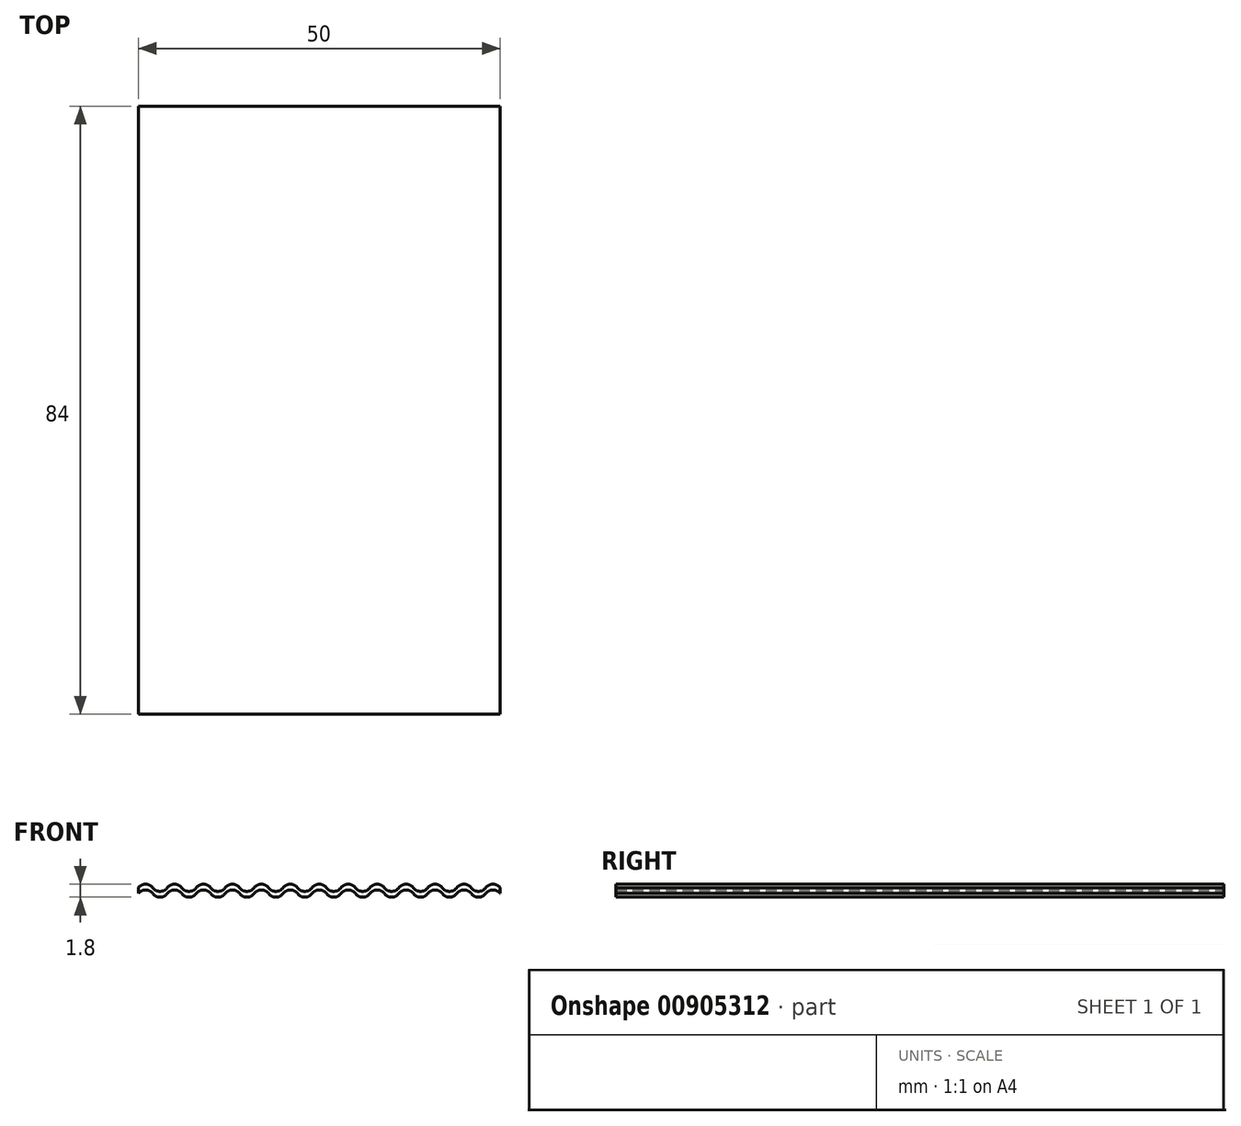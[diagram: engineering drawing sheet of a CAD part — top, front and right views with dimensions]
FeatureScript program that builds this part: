
annotation { "Feature Type Name" : "Feature", "Feature Type Description" : "" }
export const myFeature = defineFeature(function(context is Context, id is Id, definition is map)
    precondition{}
    {
        {
            var Q0;
            Q0=qCreatedBy(makeId("Front.planeOp"),FACE);
            var sketch = newSketch(context, id + "F0", { "sketchPlane" : qUnion([Q0])});
            skArc(sketch, "E0", {"start": v(-19, -0.4) * mm, "mid": v(-20, 0.1) * mm, "end": v(-21, -0.4) * mm});
            skArc(sketch, "E1", {"start": v(-23, -0.4) * mm, "mid": v(-22, -0.9) * mm, "end": v(-21, -0.4) * mm});
            skArc(sketch, "E2", {"start": v(-23, -0.4) * mm, "mid": v(-24, 0.1) * mm, "end": v(-25, -0.4) * mm});
            skArc(sketch, "E3", {"start": v(5, -0.4) * mm, "mid": v(6, -0.9) * mm, "end": v(7, -0.4) * mm});
            skArc(sketch, "E4", {"start": v(9, -0.4) * mm, "mid": v(8, 0.1) * mm, "end": v(7, -0.4) * mm});
            skArc(sketch, "E5", {"start": v(9, -0.4) * mm, "mid": v(10, -0.9) * mm, "end": v(11, -0.4) * mm});
            skArc(sketch, "E6", {"start": v(13, -0.4) * mm, "mid": v(12, 0.1) * mm, "end": v(11, -0.4) * mm});
            skArc(sketch, "E7", {"start": v(13, -0.4) * mm, "mid": v(14, -0.9) * mm, "end": v(15, -0.4) * mm});
            skArc(sketch, "E8", {"start": v(17, -0.4) * mm, "mid": v(16, 0.1) * mm, "end": v(15, -0.4) * mm});
            skArc(sketch, "E9", {"start": v(25, -0.4) * mm, "mid": v(24, 0.1) * mm, "end": v(23, -0.4) * mm});
            skArc(sketch, "E10", {"start": v(21, -0.4) * mm, "mid": v(22, -0.9) * mm, "end": v(23, -0.4) * mm});
            skArc(sketch, "E11", {"start": v(21, -0.4) * mm, "mid": v(20, 0.1) * mm, "end": v(19, -0.4) * mm});
            skArc(sketch, "E12", {"start": v(17, -0.4) * mm, "mid": v(18, -0.9) * mm, "end": v(19, -0.4) * mm});
            skArc(sketch, "E13", {"start": v(5, -0.4) * mm, "mid": v(4, 0.1) * mm, "end": v(3, -0.4) * mm});
            skArc(sketch, "E14", {"start": v(1, -0.4) * mm, "mid": v(2, -0.9) * mm, "end": v(3, -0.4) * mm});
            skArc(sketch, "E15", {"start": v(1, -0.4) * mm, "mid": v(0, 0.1) * mm, "end": v(-1, -0.4) * mm});
            skArc(sketch, "E16", {"start": v(-3, -0.4) * mm, "mid": v(-2, -0.9) * mm, "end": v(-1, -0.4) * mm});
            skArc(sketch, "E17", {"start": v(-3, -0.4) * mm, "mid": v(-4, 0.1) * mm, "end": v(-5, -0.4) * mm});
            skArc(sketch, "E18", {"start": v(-7, -0.4) * mm, "mid": v(-6, -0.9) * mm, "end": v(-5, -0.4) * mm});
            skArc(sketch, "E19", {"start": v(-7, -0.4) * mm, "mid": v(-8, 0.1) * mm, "end": v(-9, -0.4) * mm});
            skArc(sketch, "E20", {"start": v(-11, -0.4) * mm, "mid": v(-10, -0.9) * mm, "end": v(-9, -0.4) * mm});
            skArc(sketch, "E21", {"start": v(-11, -0.4) * mm, "mid": v(-12, 0.1) * mm, "end": v(-13, -0.4) * mm});
            skArc(sketch, "E22", {"start": v(-15, -0.4) * mm, "mid": v(-14, -0.9) * mm, "end": v(-13, -0.4) * mm});
            skArc(sketch, "E23", {"start": v(-15, -0.4) * mm, "mid": v(-16, 0.1) * mm, "end": v(-17, -0.4) * mm});
            skArc(sketch, "E24", {"start": v(-19, -0.4) * mm, "mid": v(-18, -0.9) * mm, "end": v(-17, -0.4) * mm});
            skArc(sketch, "E25", {"start": v(-19, 0.4) * mm, "mid": v(-20, 0.9) * mm, "end": v(-21, 0.4) * mm});
            skArc(sketch, "E26", {"start": v(-23, 0.4) * mm, "mid": v(-22, -0.1) * mm, "end": v(-21, 0.4) * mm});
            skArc(sketch, "E27", {"start": v(-23, 0.4) * mm, "mid": v(-24, 0.9) * mm, "end": v(-25, 0.4) * mm});
            skArc(sketch, "E28", {"start": v(5, 0.4) * mm, "mid": v(6, -0.1) * mm, "end": v(7, 0.4) * mm});
            skArc(sketch, "E29", {"start": v(9, 0.4) * mm, "mid": v(8, 0.9) * mm, "end": v(7, 0.4) * mm});
            skArc(sketch, "E30", {"start": v(9, 0.4) * mm, "mid": v(10, -0.1) * mm, "end": v(11, 0.4) * mm});
            skArc(sketch, "E31", {"start": v(13, 0.4) * mm, "mid": v(12, 0.9) * mm, "end": v(11, 0.4) * mm});
            skArc(sketch, "E32", {"start": v(13, 0.4) * mm, "mid": v(14, -0.1) * mm, "end": v(15, 0.4) * mm});
            skArc(sketch, "E33", {"start": v(17, 0.4) * mm, "mid": v(16, 0.9) * mm, "end": v(15, 0.4) * mm});
            skArc(sketch, "E34", {"start": v(25, 0.4) * mm, "mid": v(24, 0.9) * mm, "end": v(23, 0.4) * mm});
            skArc(sketch, "E35", {"start": v(21, 0.4) * mm, "mid": v(22, -0.1) * mm, "end": v(23, 0.4) * mm});
            skArc(sketch, "E36", {"start": v(21, 0.4) * mm, "mid": v(20, 0.9) * mm, "end": v(19, 0.4) * mm});
            skArc(sketch, "E37", {"start": v(17, 0.4) * mm, "mid": v(18, -0.1) * mm, "end": v(19, 0.4) * mm});
            skArc(sketch, "E38", {"start": v(5, 0.4) * mm, "mid": v(4, 0.9) * mm, "end": v(3, 0.4) * mm});
            skArc(sketch, "E39", {"start": v(1, 0.4) * mm, "mid": v(2, -0.1) * mm, "end": v(3, 0.4) * mm});
            skArc(sketch, "E40", {"start": v(1, 0.4) * mm, "mid": v(0, 0.9) * mm, "end": v(-1, 0.4) * mm});
            skArc(sketch, "E41", {"start": v(-3, 0.4) * mm, "mid": v(-2, -0.1) * mm, "end": v(-1, 0.4) * mm});
            skArc(sketch, "E42", {"start": v(-3, 0.4) * mm, "mid": v(-4, 0.9) * mm, "end": v(-5, 0.4) * mm});
            skArc(sketch, "E43", {"start": v(-7, 0.4) * mm, "mid": v(-6, -0.1) * mm, "end": v(-5, 0.4) * mm});
            skArc(sketch, "E44", {"start": v(-7, 0.4) * mm, "mid": v(-8, 0.9) * mm, "end": v(-9, 0.4) * mm});
            skArc(sketch, "E45", {"start": v(-11, 0.4) * mm, "mid": v(-10, -0.1) * mm, "end": v(-9, 0.4) * mm});
            skArc(sketch, "E46", {"start": v(-11, 0.4) * mm, "mid": v(-12, 0.9) * mm, "end": v(-13, 0.4) * mm});
            skArc(sketch, "E47", {"start": v(-15, 0.4) * mm, "mid": v(-14, -0.1) * mm, "end": v(-13, 0.4) * mm});
            skArc(sketch, "E48", {"start": v(-15, 0.4) * mm, "mid": v(-16, 0.9) * mm, "end": v(-17, 0.4) * mm});
            skArc(sketch, "E49", {"start": v(-19, 0.4) * mm, "mid": v(-18, -0.1) * mm, "end": v(-17, 0.4) * mm});
            skLineSegment(sketch, "E50", {"start": v(-25, 0.4) * mm, "end": v(-25, -0.4) * mm});
            skLineSegment(sketch, "E51", {"start": v(25, 0.4) * mm, "end": v(25, -0.4) * mm});
            skSolve(sketch);
        }
        {
            var Q0;
            Q0=qSketchRegion(id+"F0",true);
            extrude(context, id + "F1", {"entities" : qUnion([Q0]), "depth" : 84 * mm, "offsetDistance" : 25 * mm});
        }
    });
